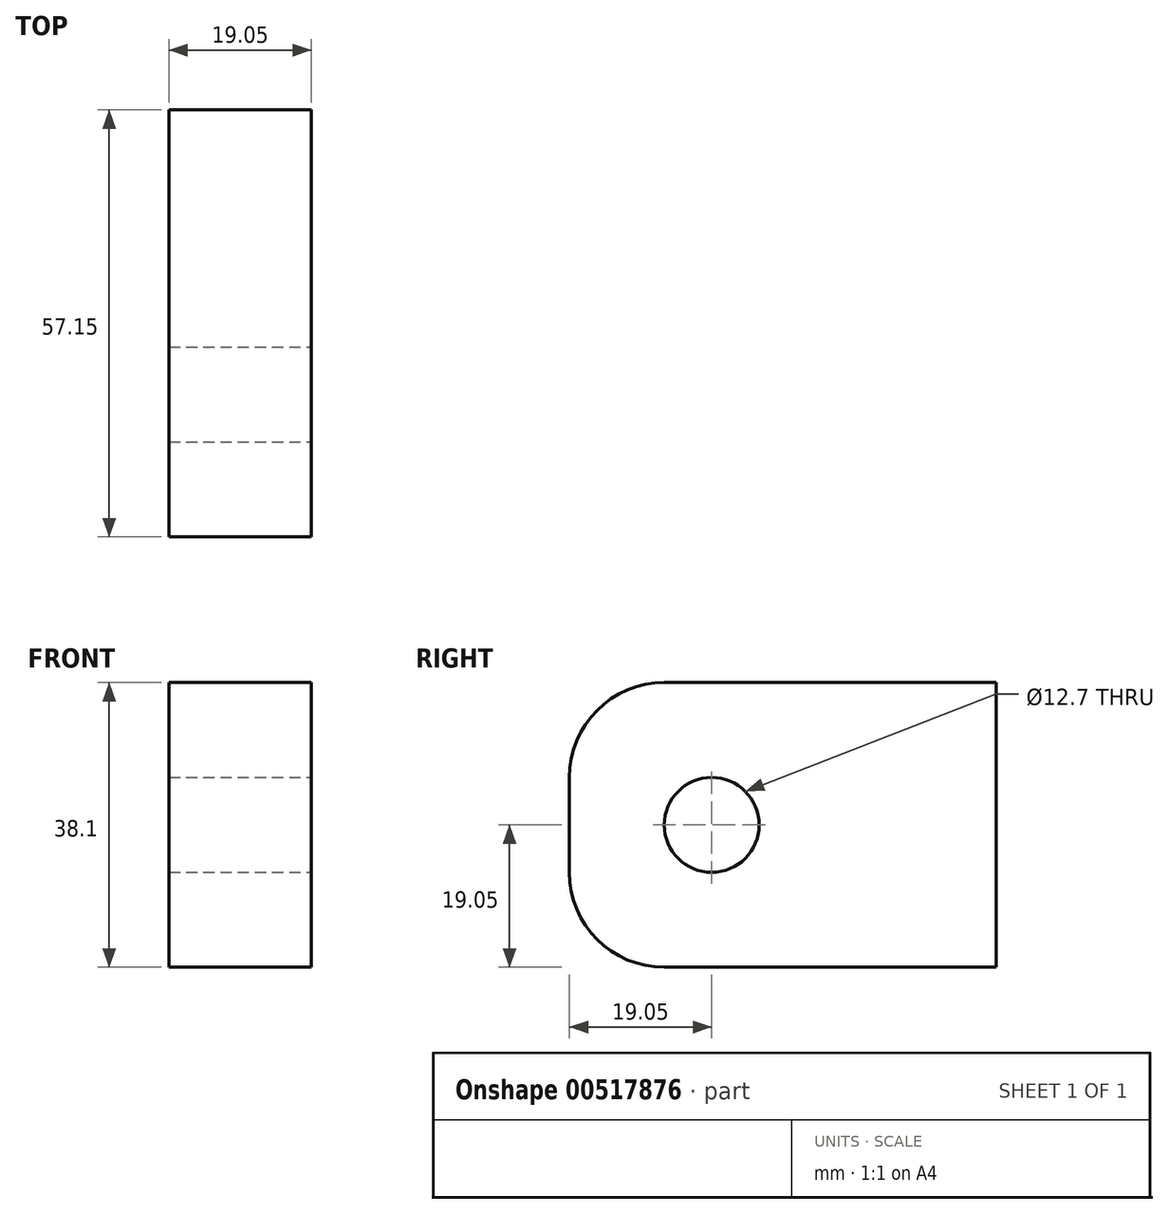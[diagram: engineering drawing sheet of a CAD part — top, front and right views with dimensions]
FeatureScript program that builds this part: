
annotation { "Feature Type Name" : "Feature", "Feature Type Description" : "" }
export const myFeature = defineFeature(function(context is Context, id is Id, definition is map)
    precondition{}
    {
        {
            var Q0;
            Q0=qCreatedBy(makeId("Right.planeOp"),FACE);
            var sketch = newSketch(context, id + "F0", { "sketchPlane" : qUnion([Q0])});
            skLineSegment(sketch, "E0.bottom", {"start": v(0, 0) * mm, "end": v(57.15, 0) * mm});
            skLineSegment(sketch, "E0.top", {"start": v(0, 38.1) * mm, "end": v(57.15, 38.1) * mm});
            skLineSegment(sketch, "E0.left", {"start": v(0, 0) * mm, "end": v(0, 38.1) * mm});
            skLineSegment(sketch, "E0.right", {"start": v(57.15, 0) * mm, "end": v(57.15, 38.1) * mm});
            skCircle(sketch, "E1", {"center": v(0, 19.05) * mm, "radius": 6.35 * mm, "construction": true});
            skCircle(sketch, "E2.1.0.0", {"center": v(19.05, 19.05) * mm, "radius": 6.35 * mm});
            skLineSegment(sketch, "E2.direction1", {"start": v(0, 19.05) * mm, "end": v(19.05, 19.05) * mm, "construction": true});
            skSolve(sketch);
        }
        {
            var Q0;
            Q0=makeQuery(id+"F0.imprint","IMPRINT",FACE,{"disambiguationData":[TD([[makeQuery(id+"F0.imprint","IMPRINT",EDGE,{"derivedFrom":sQuery(id+"F0.wireOp",EDGE,"E0.bottom")}),1.0]])]});
            extrude(context, id + "F1", {"entities" : qUnion([Q0]), "oppositeDirection" : true, "depth" : 19.05 * mm, "offsetDistance" : 25.4 * mm});
        }
        {
            var Q0;
            Q0=makeQuery(id+"F1.opExtrude","SWEPT_EDGE",EDGE,{"disambiguationData":[OSD([sQuery(id+"F0.wireOp",EDGE,"E0.bottom"),sQuery(id+"F0.wireOp",EDGE,"E0.left")])]});
            var Q1;
            Q1=makeQuery(id+"F1.opExtrude","SWEPT_EDGE",EDGE,{"disambiguationData":[OSD([sQuery(id+"F0.wireOp",EDGE,"E0.top"),sQuery(id+"F0.wireOp",EDGE,"E0.left")])]});
            fillet(context, id + "F2", {"entities" : qUnion([Q0, Q1]), "radius" : 12.7 * mm, "tangentPropagation" : true, "allowEdgeOverflow" : false});
        }
    });
